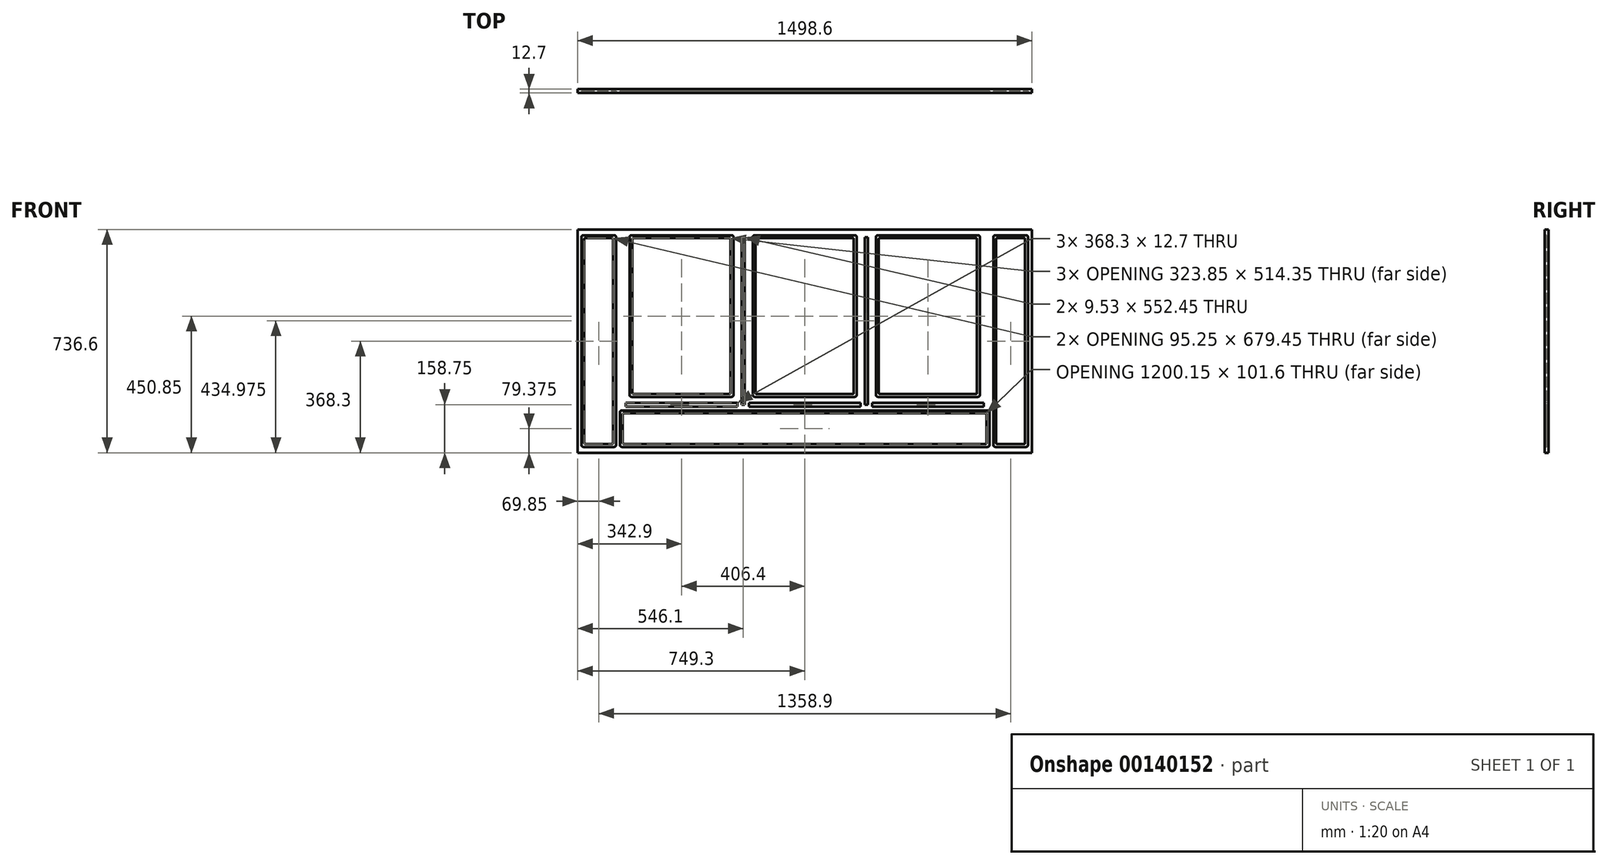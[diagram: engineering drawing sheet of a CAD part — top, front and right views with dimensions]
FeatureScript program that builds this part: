
annotation { "Feature Type Name" : "Feature", "Feature Type Description" : "" }
export const myFeature = defineFeature(function(context is Context, id is Id, definition is map)
    precondition{}
    {
        {
            var Q0;
            Q0=qCreatedBy(makeId("Front.planeOp"),FACE);
            var sketch = newSketch(context, id + "F0", { "sketchPlane" : qUnion([Q0])});
            skLineSegment(sketch, "E0", {"start": v(-622.3, 723.9) * mm, "end": v(-622.3, 38.1) * mm});
            skLineSegment(sketch, "E1", {"start": v(-609.6, 146.05) * mm, "end": v(-609.6, 38.1) * mm});
            skLineSegment(sketch, "E2", {"start": v(622.3, 723.9) * mm, "end": v(622.3, 38.1) * mm});
            skLineSegment(sketch, "E3", {"start": v(609.6, 146.05) * mm, "end": v(609.6, 38.1) * mm});
            skLineSegment(sketch, "E4.MirrorCS", {"start": v(-577.85, 723.9) * mm, "end": v(-577.85, 203.2) * mm});
            skLineSegment(sketch, "E5.MirrorCS", {"start": v(-234.95, 723.9) * mm, "end": v(-234.95, 203.2) * mm});
            skLineSegment(sketch, "E6", {"start": v(-171.45, 723.9) * mm, "end": v(-171.45, 203.2) * mm});
            skLineSegment(sketch, "E7", {"start": v(171.45, 723.9) * mm, "end": v(171.45, 203.2) * mm});
            skLineSegment(sketch, "E8", {"start": v(234.95, 723.9) * mm, "end": v(234.95, 203.2) * mm});
            skLineSegment(sketch, "E9", {"start": v(577.85, 723.9) * mm, "end": v(577.85, 203.2) * mm});
            skLineSegment(sketch, "E10", {"start": v(241.3, 730.25) * mm, "end": v(571.5, 730.25) * mm});
            skLineSegment(sketch, "E11", {"start": v(-165.1, 730.25) * mm, "end": v(165.1, 730.25) * mm});
            skLineSegment(sketch, "E12", {"start": v(-571.5, 730.25) * mm, "end": v(-241.3, 730.25) * mm});
            skPoint(sketch, "E13.visualSharp", {"position": v(-577.85, 730.25) * mm});
            skArc(sketch, "E13.filletArc", {"start": v(-571.5, 730.25) * mm, "mid": v(-576, 728.4) * mm, "end": v(-577.85, 723.9) * mm});
            skPoint(sketch, "E14.visualSharp", {"position": v(-234.95, 730.25) * mm});
            skArc(sketch, "E14.filletArc", {"start": v(-234.95, 723.9) * mm, "mid": v(-236.8, 728.4) * mm, "end": v(-241.3, 730.25) * mm});
            skPoint(sketch, "E15.visualSharp", {"position": v(577.85, 730.25) * mm});
            skArc(sketch, "E15.filletArc", {"start": v(577.85, 723.9) * mm, "mid": v(576, 728.4) * mm, "end": v(571.5, 730.25) * mm});
            skPoint(sketch, "E16.visualSharp", {"position": v(234.95, 730.25) * mm});
            skArc(sketch, "E16.filletArc", {"start": v(241.3, 730.25) * mm, "mid": v(236.8, 728.4) * mm, "end": v(234.95, 723.9) * mm});
            skPoint(sketch, "E17.visualSharp", {"position": v(171.45, 730.25) * mm});
            skArc(sketch, "E17.filletArc", {"start": v(171.45, 723.9) * mm, "mid": v(169.6, 728.4) * mm, "end": v(165.1, 730.25) * mm});
            skPoint(sketch, "E18.visualSharp", {"position": v(-171.45, 730.25) * mm});
            skArc(sketch, "E18.filletArc", {"start": v(-165.1, 730.25) * mm, "mid": v(-169.6, 728.4) * mm, "end": v(-171.45, 723.9) * mm});
            skLineSegment(sketch, "E19", {"start": v(-571.5, 196.85) * mm, "end": v(-241.3, 196.85) * mm});
            skPoint(sketch, "E20.visualSharp", {"position": v(-577.85, 196.85) * mm});
            skArc(sketch, "E20.filletArc", {"start": v(-577.85, 203.2) * mm, "mid": v(-576, 198.7) * mm, "end": v(-571.5, 196.85) * mm});
            skPoint(sketch, "E21.visualSharp", {"position": v(-234.95, 196.85) * mm});
            skArc(sketch, "E21.filletArc", {"start": v(-241.3, 196.85) * mm, "mid": v(-236.8, 198.7) * mm, "end": v(-234.95, 203.2) * mm});
            skLineSegment(sketch, "E22", {"start": v(-749.3, 12.7) * mm, "end": v(-749.3, 749.3) * mm});
            skLineSegment(sketch, "E23", {"start": v(749.3, 12.7) * mm, "end": v(749.3, 749.3) * mm});
            skLineSegment(sketch, "E24.trimOffspring", {"start": v(603.25, 152.4) * mm, "end": v(-603.25, 152.4) * mm});
            skLineSegment(sketch, "E25", {"start": v(-207.96, 723.9) * mm, "end": v(-198.44, 723.9) * mm});
            skLineSegment(sketch, "E26", {"start": v(198.44, 723.9) * mm, "end": v(207.96, 723.9) * mm});
            skLineSegment(sketch, "E27", {"start": v(736.6, 723.9) * mm, "end": v(736.6, 38.1) * mm});
            skLineSegment(sketch, "E28", {"start": v(-600.08, 139.7) * mm, "end": v(-600.08, 44.45) * mm});
            skLineSegment(sketch, "E29", {"start": v(600.08, 44.45) * mm, "end": v(600.08, 139.7) * mm});
            skLineSegment(sketch, "E30", {"start": v(-596.9, 142.87) * mm, "end": v(596.9, 142.87) * mm});
            skLineSegment(sketch, "E31.0", {"start": v(-568.33, 717.55) * mm, "end": v(-568.33, 209.55) * mm});
            skLineSegment(sketch, "E31.1", {"start": v(-565.15, 720.73) * mm, "end": v(-247.65, 720.73) * mm});
            skLineSegment(sketch, "E31.2", {"start": v(-244.48, 717.55) * mm, "end": v(-244.48, 209.55) * mm});
            skLineSegment(sketch, "E31.3", {"start": v(-565.15, 206.37) * mm, "end": v(-247.65, 206.37) * mm});
            skLineSegment(sketch, "E32.0", {"start": v(-158.75, 720.73) * mm, "end": v(158.75, 720.73) * mm});
            skLineSegment(sketch, "E32.1", {"start": v(-161.93, 717.55) * mm, "end": v(-161.92, 209.55) * mm});
            skLineSegment(sketch, "E32.3", {"start": v(161.93, 717.55) * mm, "end": v(161.93, 209.55) * mm});
            skLineSegment(sketch, "E33.0", {"start": v(244.48, 717.55) * mm, "end": v(244.48, 209.55) * mm});
            skLineSegment(sketch, "E33.1", {"start": v(247.65, 720.73) * mm, "end": v(565.15, 720.73) * mm});
            skLineSegment(sketch, "E33.2", {"start": v(568.33, 717.55) * mm, "end": v(568.33, 209.55) * mm});
            skPoint(sketch, "E34.visualSharp", {"position": v(244.48, 720.73) * mm});
            skArc(sketch, "E34.filletArc", {"start": v(247.65, 720.73) * mm, "mid": v(245.4, 719.8) * mm, "end": v(244.48, 717.55) * mm});
            skPoint(sketch, "E35.visualSharp", {"position": v(568.33, 720.73) * mm});
            skArc(sketch, "E35.filletArc", {"start": v(568.33, 717.55) * mm, "mid": v(567.4, 719.8) * mm, "end": v(565.15, 720.73) * mm});
            skPoint(sketch, "E36.visualSharp", {"position": v(161.93, 720.73) * mm});
            skArc(sketch, "E36.filletArc", {"start": v(161.93, 717.55) * mm, "mid": v(161, 719.8) * mm, "end": v(158.75, 720.73) * mm});
            skPoint(sketch, "E37.visualSharp", {"position": v(-161.93, 720.73) * mm});
            skArc(sketch, "E37.filletArc", {"start": v(-158.75, 720.73) * mm, "mid": v(-161, 719.8) * mm, "end": v(-161.93, 717.55) * mm});
            skPoint(sketch, "E38.visualSharp", {"position": v(-244.48, 720.73) * mm});
            skArc(sketch, "E38.filletArc", {"start": v(-244.48, 717.55) * mm, "mid": v(-245.4, 719.8) * mm, "end": v(-247.65, 720.73) * mm});
            skPoint(sketch, "E39.visualSharp", {"position": v(-244.48, 206.37) * mm});
            skArc(sketch, "E39.filletArc", {"start": v(-247.65, 206.37) * mm, "mid": v(-245.4, 207.3) * mm, "end": v(-244.48, 209.55) * mm});
            skPoint(sketch, "E40.visualSharp", {"position": v(-568.33, 206.37) * mm});
            skArc(sketch, "E40.filletArc", {"start": v(-568.33, 209.55) * mm, "mid": v(-567.4, 207.3) * mm, "end": v(-565.15, 206.37) * mm});
            skPoint(sketch, "E41.visualSharp", {"position": v(-568.33, 720.73) * mm});
            skArc(sketch, "E41.filletArc", {"start": v(-565.15, 720.73) * mm, "mid": v(-567.4, 719.8) * mm, "end": v(-568.33, 717.55) * mm});
            skLineSegment(sketch, "E42", {"start": v(631.83, 44.45) * mm, "end": v(631.83, 717.55) * mm});
            skLineSegment(sketch, "E43", {"start": v(727.07, 44.45) * mm, "end": v(727.07, 717.55) * mm});
            skArc(sketch, "E44.filletArc", {"start": v(-603.25, 152.4) * mm, "mid": v(-607.74, 150.54) * mm, "end": v(-609.6, 146.05) * mm});
            skPoint(sketch, "E45.visualSharp", {"position": v(600.08, 142.87) * mm});
            skPoint(sketch, "E46.visualSharp", {"position": v(-600.08, 142.87) * mm});
            skArc(sketch, "E46.filletArc", {"start": v(-596.9, 142.87) * mm, "mid": v(-599.15, 141.95) * mm, "end": v(-600.08, 139.7) * mm});
            skArc(sketch, "E47.filletArc", {"start": v(609.6, 146.05) * mm, "mid": v(607.74, 150.54) * mm, "end": v(603.25, 152.4) * mm});
            skArc(sketch, "E48.filletArc", {"start": v(600.08, 139.7) * mm, "mid": v(599.15, 141.95) * mm, "end": v(596.9, 142.87) * mm});
            skLineSegment(sketch, "E49.trimOffspring", {"start": v(635, 720.72) * mm, "end": v(723.9, 720.72) * mm});
            skLineSegment(sketch, "E50.trimOffspring", {"start": v(628.65, 730.25) * mm, "end": v(730.25, 730.25) * mm});
            skPoint(sketch, "E51.visualSharp", {"position": v(727.07, 720.72) * mm});
            skArc(sketch, "E51.filletArc", {"start": v(727.07, 717.55) * mm, "mid": v(726.15, 719.8) * mm, "end": v(723.9, 720.72) * mm});
            skPoint(sketch, "E52.visualSharp", {"position": v(631.83, 720.72) * mm});
            skArc(sketch, "E52.filletArc", {"start": v(635, 720.72) * mm, "mid": v(632.75, 719.8) * mm, "end": v(631.83, 717.55) * mm});
            skPoint(sketch, "E53.visualSharp", {"position": v(622.3, 730.25) * mm});
            skPoint(sketch, "E54.visualSharp", {"position": v(736.6, 730.25) * mm});
            skArc(sketch, "E55.filletArc", {"start": v(736.6, 723.9) * mm, "mid": v(734.74, 728.4) * mm, "end": v(730.25, 730.25) * mm});
            skArc(sketch, "E56.filletArc", {"start": v(628.65, 730.25) * mm, "mid": v(624.16, 728.4) * mm, "end": v(622.3, 723.9) * mm});
            skLineSegment(sketch, "E57.trimOffspring", {"start": v(-631.82, 717.55) * mm, "end": v(-631.82, 44.45) * mm});
            skLineSegment(sketch, "E58.trimOffspring", {"start": v(-628.65, 730.25) * mm, "end": v(-730.25, 730.25) * mm});
            skLineSegment(sketch, "E59.trimOffspring", {"start": v(-635, 720.73) * mm, "end": v(-723.9, 720.73) * mm});
            skPoint(sketch, "E60.visualSharp", {"position": v(-622.3, 730.25) * mm});
            skArc(sketch, "E60.filletArc", {"start": v(-622.3, 723.9) * mm, "mid": v(-624.16, 728.4) * mm, "end": v(-628.65, 730.25) * mm});
            skPoint(sketch, "E61.visualSharp", {"position": v(-631.82, 720.73) * mm});
            skArc(sketch, "E61.filletArc", {"start": v(-631.82, 717.55) * mm, "mid": v(-632.75, 719.8) * mm, "end": v(-635, 720.73) * mm});
            skLineSegment(sketch, "E62", {"start": v(749.3, 12.7) * mm, "end": v(-749.3, 12.7) * mm});
            skLineSegment(sketch, "E63", {"start": v(-730.25, 31.75) * mm, "end": v(-628.65, 31.75) * mm});
            skLineSegment(sketch, "E64.trimOffspring", {"start": v(-596.9, 41.27) * mm, "end": v(596.9, 41.27) * mm});
            skLineSegment(sketch, "E65.trimOffspring", {"start": v(-723.9, 41.27) * mm, "end": v(-635, 41.27) * mm});
            skLineSegment(sketch, "E66.trimOffspring", {"start": v(635, 41.27) * mm, "end": v(723.9, 41.27) * mm});
            skLineSegment(sketch, "E67.trimOffspring", {"start": v(628.65, 31.75) * mm, "end": v(730.25, 31.75) * mm});
            skLineSegment(sketch, "E68.trimOffspring", {"start": v(-603.25, 31.75) * mm, "end": v(603.25, 31.75) * mm});
            skPoint(sketch, "E69.visualSharp", {"position": v(-600.08, 41.27) * mm});
            skArc(sketch, "E69.filletArc", {"start": v(-600.08, 44.45) * mm, "mid": v(-599.15, 42.2) * mm, "end": v(-596.9, 41.27) * mm});
            skPoint(sketch, "E70.visualSharp", {"position": v(600.08, 41.27) * mm});
            skArc(sketch, "E70.filletArc", {"start": v(596.9, 41.27) * mm, "mid": v(599.15, 42.2) * mm, "end": v(600.08, 44.45) * mm});
            skPoint(sketch, "E71.visualSharp", {"position": v(609.6, 31.75) * mm});
            skArc(sketch, "E71.filletArc", {"start": v(603.25, 31.75) * mm, "mid": v(607.74, 33.6) * mm, "end": v(609.6, 38.1) * mm});
            skPoint(sketch, "E72.visualSharp", {"position": v(-609.6, 31.75) * mm});
            skArc(sketch, "E72.filletArc", {"start": v(-609.6, 38.1) * mm, "mid": v(-607.74, 33.6) * mm, "end": v(-603.25, 31.75) * mm});
            skPoint(sketch, "E73.visualSharp", {"position": v(-622.3, 31.75) * mm});
            skArc(sketch, "E73.filletArc", {"start": v(-628.65, 31.75) * mm, "mid": v(-624.16, 33.6) * mm, "end": v(-622.3, 38.1) * mm});
            skPoint(sketch, "E74.visualSharp", {"position": v(-631.82, 41.27) * mm});
            skArc(sketch, "E74.filletArc", {"start": v(-635, 41.27) * mm, "mid": v(-632.75, 42.2) * mm, "end": v(-631.82, 44.45) * mm});
            skPoint(sketch, "E75.visualSharp", {"position": v(622.3, 31.75) * mm});
            skArc(sketch, "E75.filletArc", {"start": v(622.3, 38.1) * mm, "mid": v(624.16, 33.6) * mm, "end": v(628.65, 31.75) * mm});
            skPoint(sketch, "E76.visualSharp", {"position": v(736.6, 31.75) * mm});
            skArc(sketch, "E76.filletArc", {"start": v(730.25, 31.75) * mm, "mid": v(734.74, 33.6) * mm, "end": v(736.6, 38.1) * mm});
            skPoint(sketch, "E77.visualSharp", {"position": v(631.83, 41.27) * mm});
            skArc(sketch, "E77.filletArc", {"start": v(631.83, 44.45) * mm, "mid": v(632.75, 42.2) * mm, "end": v(635, 41.27) * mm});
            skPoint(sketch, "E78.visualSharp", {"position": v(727.07, 41.27) * mm});
            skArc(sketch, "E78.filletArc", {"start": v(723.9, 41.27) * mm, "mid": v(726.15, 42.2) * mm, "end": v(727.07, 44.45) * mm});
            skLineSegment(sketch, "E79", {"start": v(-590.55, 177.8) * mm, "end": v(-222.25, 177.8) * mm});
            skLineSegment(sketch, "E80", {"start": v(222.25, 165.1) * mm, "end": v(222.25, 177.8) * mm});
            skLineSegment(sketch, "E81", {"start": v(184.15, 165.1) * mm, "end": v(184.15, 177.8) * mm});
            skLineSegment(sketch, "E82", {"start": v(-222.25, 165.1) * mm, "end": v(-222.25, 177.8) * mm});
            skLineSegment(sketch, "E83", {"start": v(-184.15, 165.1) * mm, "end": v(-184.15, 177.8) * mm});
            skLineSegment(sketch, "E84", {"start": v(-590.55, 177.8) * mm, "end": v(-590.55, 165.1) * mm});
            skLineSegment(sketch, "E85.trimOffspring", {"start": v(-158.75, 206.37) * mm, "end": v(158.75, 206.37) * mm});
            skLineSegment(sketch, "E86.trimOffspring", {"start": v(-165.1, 196.85) * mm, "end": v(165.1, 196.85) * mm});
            skLineSegment(sketch, "E87.trimOffspring", {"start": v(241.3, 196.85) * mm, "end": v(571.5, 196.85) * mm});
            skLineSegment(sketch, "E88.trimOffspring", {"start": v(247.65, 206.37) * mm, "end": v(565.15, 206.37) * mm});
            skPoint(sketch, "E89.visualSharp", {"position": v(-171.45, 196.85) * mm});
            skArc(sketch, "E89.filletArc", {"start": v(-171.45, 203.2) * mm, "mid": v(-169.6, 198.7) * mm, "end": v(-165.1, 196.85) * mm});
            skPoint(sketch, "E90.visualSharp", {"position": v(171.45, 196.85) * mm});
            skArc(sketch, "E90.filletArc", {"start": v(165.1, 196.85) * mm, "mid": v(169.6, 198.7) * mm, "end": v(171.45, 203.2) * mm});
            skPoint(sketch, "E91.visualSharp", {"position": v(234.95, 196.85) * mm});
            skArc(sketch, "E91.filletArc", {"start": v(234.95, 203.2) * mm, "mid": v(236.8, 198.7) * mm, "end": v(241.3, 196.85) * mm});
            skPoint(sketch, "E92.visualSharp", {"position": v(577.85, 196.85) * mm});
            skArc(sketch, "E92.filletArc", {"start": v(571.5, 196.85) * mm, "mid": v(576, 198.7) * mm, "end": v(577.85, 203.2) * mm});
            skPoint(sketch, "E93.visualSharp", {"position": v(244.48, 206.37) * mm});
            skArc(sketch, "E93.filletArc", {"start": v(244.48, 209.55) * mm, "mid": v(245.4, 207.3) * mm, "end": v(247.65, 206.37) * mm});
            skPoint(sketch, "E94.visualSharp", {"position": v(568.33, 206.37) * mm});
            skArc(sketch, "E94.filletArc", {"start": v(565.15, 206.37) * mm, "mid": v(567.4, 207.3) * mm, "end": v(568.32, 209.55) * mm});
            skPoint(sketch, "E95.visualSharp", {"position": v(161.93, 206.37) * mm});
            skArc(sketch, "E95.filletArc", {"start": v(158.75, 206.37) * mm, "mid": v(161, 207.3) * mm, "end": v(161.93, 209.55) * mm});
            skPoint(sketch, "E96.visualSharp", {"position": v(-161.92, 206.37) * mm});
            skArc(sketch, "E96.filletArc", {"start": v(-161.92, 209.55) * mm, "mid": v(-161, 207.3) * mm, "end": v(-158.75, 206.37) * mm});
            skLineSegment(sketch, "E97", {"start": v(-207.96, 171.45) * mm, "end": v(-207.96, 723.9) * mm});
            skLineSegment(sketch, "E98", {"start": v(-198.44, 171.45) * mm, "end": v(-198.44, 723.9) * mm});
            skLineSegment(sketch, "E99", {"start": v(198.44, 171.45) * mm, "end": v(198.44, 723.9) * mm});
            skLineSegment(sketch, "E100", {"start": v(207.96, 171.45) * mm, "end": v(207.96, 723.9) * mm});
            skLineSegment(sketch, "E101", {"start": v(-749.3, 749.3) * mm, "end": v(749.3, 749.3) * mm});
            skLineSegment(sketch, "E102", {"start": v(-727.07, 717.55) * mm, "end": v(-727.07, 44.45) * mm});
            skLineSegment(sketch, "E103", {"start": v(-736.6, 38.1) * mm, "end": v(-736.6, 723.9) * mm});
            skPoint(sketch, "E104.visualSharp", {"position": v(-727.07, 41.27) * mm});
            skArc(sketch, "E104.filletArc", {"start": v(-727.07, 44.45) * mm, "mid": v(-726.15, 42.2) * mm, "end": v(-723.9, 41.27) * mm});
            skPoint(sketch, "E105.visualSharp", {"position": v(-727.07, 720.73) * mm});
            skArc(sketch, "E105.filletArc", {"start": v(-723.9, 720.73) * mm, "mid": v(-726.15, 719.8) * mm, "end": v(-727.07, 717.55) * mm});
            skPoint(sketch, "E106.visualSharp", {"position": v(-736.6, 31.75) * mm});
            skArc(sketch, "E106.filletArc", {"start": v(-736.6, 38.1) * mm, "mid": v(-734.74, 33.6) * mm, "end": v(-730.25, 31.75) * mm});
            skPoint(sketch, "E107.visualSharp", {"position": v(-736.6, 730.25) * mm});
            skArc(sketch, "E107.filletArc", {"start": v(-730.25, 730.25) * mm, "mid": v(-734.74, 728.4) * mm, "end": v(-736.6, 723.9) * mm});
            skLineSegment(sketch, "E108.trimOffspring", {"start": v(-184.15, 177.8) * mm, "end": v(184.15, 177.8) * mm});
            skLineSegment(sketch, "E109", {"start": v(-207.96, 171.45) * mm, "end": v(-198.44, 171.45) * mm});
            skLineSegment(sketch, "E110.trimOffspring", {"start": v(222.25, 177.8) * mm, "end": v(590.55, 177.8) * mm});
            skLineSegment(sketch, "E111", {"start": v(198.44, 171.45) * mm, "end": v(207.96, 171.45) * mm});
            skLineSegment(sketch, "E112", {"start": v(-590.55, 165.1) * mm, "end": v(-222.25, 165.1) * mm});
            skLineSegment(sketch, "E113", {"start": v(-184.15, 165.1) * mm, "end": v(184.15, 165.1) * mm});
            skLineSegment(sketch, "E114", {"start": v(222.25, 165.1) * mm, "end": v(590.55, 165.1) * mm});
            skLineSegment(sketch, "E115", {"start": v(590.55, 177.8) * mm, "end": v(590.55, 165.1) * mm});
            skSolve(sketch);
        }
        {
            var Q0;
            Q0=makeQuery(id+"F0.imprint","IMPRINT",FACE,{"disambiguationData":[TD([[makeQuery(id+"F0.imprint","IMPRINT",EDGE,{"derivedFrom":sQuery(id+"F0.wireOp",EDGE,"E0")}),1.0]])]});
            var Q1;
            Q1=makeQuery(id+"F0.imprint","IMPRINT",FACE,{"disambiguationData":[TD([[makeQuery(id+"F0.imprint","IMPRINT",EDGE,{"derivedFrom":sQuery(id+"F0.wireOp",EDGE,"E0")}),-1.0]])]});
            var Q2;
            Q2=makeQuery(id+"F0.imprint","IMPRINT",FACE,{"disambiguationData":[TD([[makeQuery(id+"F0.imprint","IMPRINT",EDGE,{"derivedFrom":sQuery(id+"F0.wireOp",EDGE,"E4.MirrorCS")}),1.0]])]});
            var Q3;
            Q3=makeQuery(id+"F0.imprint","IMPRINT",FACE,{"disambiguationData":[TD([[makeQuery(id+"F0.imprint","IMPRINT",EDGE,{"derivedFrom":sQuery(id+"F0.wireOp",EDGE,"E6")}),1.0]])]});
            var Q4;
            Q4=makeQuery(id+"F0.imprint","IMPRINT",FACE,{"disambiguationData":[TD([[makeQuery(id+"F0.imprint","IMPRINT",EDGE,{"derivedFrom":sQuery(id+"F0.wireOp",EDGE,"E8")}),1.0]])]});
            var Q5;
            Q5=makeQuery(id+"F0.imprint","IMPRINT",FACE,{"disambiguationData":[TD([[makeQuery(id+"F0.imprint","IMPRINT",EDGE,{"derivedFrom":sQuery(id+"F0.wireOp",EDGE,"E2")}),1.0]])]});
            var Q6;
            Q6=makeQuery(id+"F0.imprint","IMPRINT",FACE,{"disambiguationData":[TD([[makeQuery(id+"F0.imprint","IMPRINT",EDGE,{"derivedFrom":sQuery(id+"F0.wireOp",EDGE,"E1")}),1.0]])]});
            extrude(context, id + "F1", {"entities" : qUnion([Q0, Q1, Q2, Q3, Q4, Q5, Q6]), "oppositeDirection" : true, "depth" : 12.7 * mm});
        }
        {
            var Q0;
            Q0=makeQuery(id+"F0.imprint","IMPRINT",FACE,{"disambiguationData":[TD([[makeQuery(id+"F0.imprint","IMPRINT",EDGE,{"derivedFrom":sQuery(id+"F0.wireOp",EDGE,"E0")}),-1.0]])]});
            var Q1;
            Q1=makeQuery(id+"F0.imprint","IMPRINT",FACE,{"disambiguationData":[TD([[makeQuery(id+"F0.imprint","IMPRINT",EDGE,{"derivedFrom":sQuery(id+"F0.wireOp",EDGE,"E4.MirrorCS")}),1.0]])]});
            var Q2;
            Q2=makeQuery(id+"F0.imprint","IMPRINT",FACE,{"disambiguationData":[TD([[makeQuery(id+"F0.imprint","IMPRINT",EDGE,{"derivedFrom":sQuery(id+"F0.wireOp",EDGE,"E6")}),1.0]])]});
            var Q3;
            Q3=makeQuery(id+"F0.imprint","IMPRINT",FACE,{"disambiguationData":[TD([[makeQuery(id+"F0.imprint","IMPRINT",EDGE,{"derivedFrom":sQuery(id+"F0.wireOp",EDGE,"E8")}),1.0]])]});
            var Q4;
            Q4=makeQuery(id+"F0.imprint","IMPRINT",FACE,{"disambiguationData":[TD([[makeQuery(id+"F0.imprint","IMPRINT",EDGE,{"derivedFrom":sQuery(id+"F0.wireOp",EDGE,"E2")}),1.0]])]});
            var Q5;
            Q5=makeQuery(id+"F0.imprint","IMPRINT",FACE,{"disambiguationData":[TD([[makeQuery(id+"F0.imprint","IMPRINT",EDGE,{"derivedFrom":sQuery(id+"F0.wireOp",EDGE,"E1")}),1.0]])]});
            extrude(context, id + "F2", {"entities" : qUnion([Q0, Q1, Q2, Q3, Q4, Q5]), "operationType" : NewBodyOperationType.REMOVE, "oppositeDirection" : true, "depth" : 6.35 * mm});
        }
    });
